# Revit family: Torno Table Round
name_source: partatom
category: Furniture
revit_build: Autodesk Revit 2017 (Build: 20171027_0315(x64)
units: mm (PartAtom-declared; Revit-internal decimal feet)

## family parameters
Always vertical = Yes
Cut with Voids When Loaded = No
OmniClass Number = 23.40.20.00
OmniClass Title = General Furniture and Specialties
Room Calculation Point = No
Shared = No
Work Plane-Based = No

## types (1)
- Torno Table Round
    Designer = Form Us With Love
    Diameter (cm) = 75
    Diameter (in) = 29,5
    Feet = +Halle Pom - black
    Frame = +Halle Powdercoated aluminium - RAL 6028
    Height (cm) = 73
    Height (in) = 28,7
    Packaging Dimensions (cm) = 77 / 77 / 76
    Packaging Dimensions (in) = 30.3 / 30.3 / 29.9
    Product family = Torno
    Table top = +Halle Powdercoated aluminium - RAL 6028
    URL = https://www.plushalle.com
    Warranty period = 2 years standard warranty
    Weight (kg) = 9,5
    Weight (lbs) = 20,9

## geometry (parser evidence)
native form markers: Sweep x2
no freeform markers — native parametric forms only
